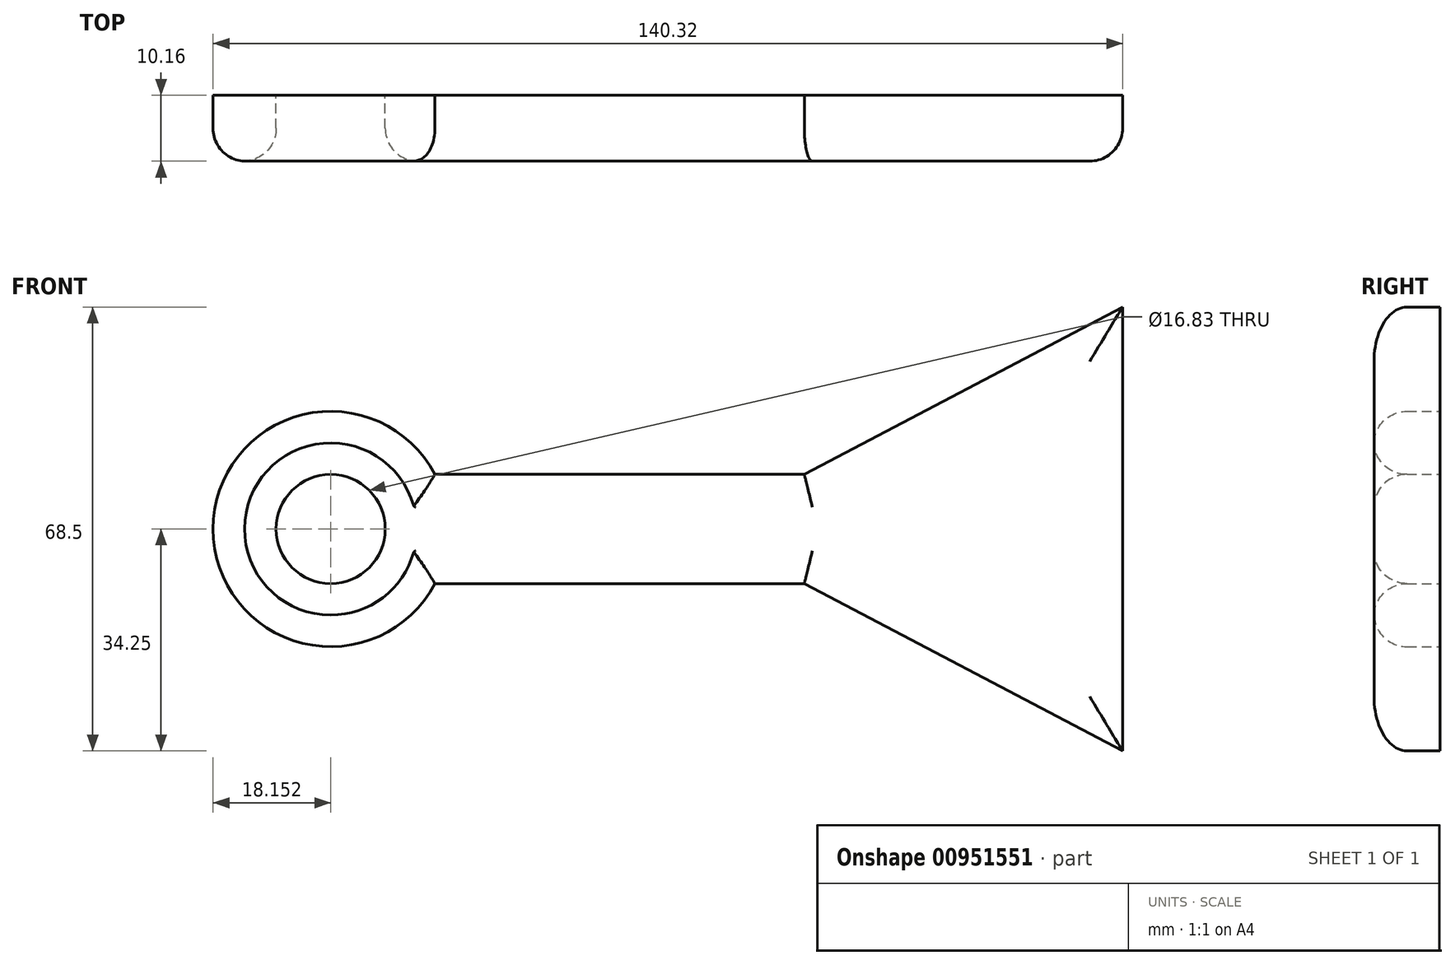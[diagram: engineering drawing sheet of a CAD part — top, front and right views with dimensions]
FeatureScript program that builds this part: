
annotation { "Feature Type Name" : "Feature", "Feature Type Description" : "" }
export const myFeature = defineFeature(function(context is Context, id is Id, definition is map)
    precondition{}
    {
        {
            var Q0;
            Q0=qCreatedBy(makeId("Front.planeOp"),FACE);
            var sketch = newSketch(context, id + "F0", { "sketchPlane" : qUnion([Q0])});
            skCircle(sketch, "E0", {"center": v(-109.18, 0) * mm, "radius": 8.42 * mm});
            skCircle(sketch, "E1", {"center": v(-109.18, 0) * mm, "radius": 18.16 * mm});
            skLineSegment(sketch, "E2", {"start": v(-109.18, 8.42) * mm, "end": v(0, 8.42) * mm});
            skLineSegment(sketch, "E3", {"start": v(0, 8.42) * mm, "end": v(0, -8.42) * mm});
            skLineSegment(sketch, "E4", {"start": v(0, -8.42) * mm, "end": v(-109.18, -8.42) * mm});
            skLineSegment(sketch, "E5", {"start": v(-36.11, 8.42) * mm, "end": v(12.99, 34.25) * mm});
            skLineSegment(sketch, "E6", {"start": v(12.99, 34.25) * mm, "end": v(12.99, -34.25) * mm});
            skLineSegment(sketch, "E7", {"start": v(12.99, -34.25) * mm, "end": v(-36.11, -8.42) * mm});
            skSolve(sketch);
        }
        {
            var Q0;
            Q0 = qSketchRegion(id + "F0", true);
            extrude(context, id + "F1", {"entities" : qUnion([Q0]), "depth" : 10.16 * mm, "offsetDistance" : 25.4 * mm});
        }
        {
            var Q0;
            Q0=makeQuery(id+"F1.opExtrude","CAP_FACE",FACE,{"disambiguationData":[OSD([sQuery(id+"F0.wireOp",EDGE,"E0"),sQuery(id+"F0.wireOp",EDGE,"E1"),sQuery(id+"F0.wireOp",EDGE,"E2"),sQuery(id+"F0.wireOp",EDGE,"E4"),sQuery(id+"F0.wireOp",EDGE,"E5"),sQuery(id+"F0.wireOp",EDGE,"E6"),sQuery(id+"F0.wireOp",EDGE,"E7")])],"isStart":false});
            fillet(context, id + "F2", {"entities" : qUnion([Q0]), "radius" : 5.08 * mm, "tangentPropagation" : true, "allowEdgeOverflow" : false});
        }
    });
